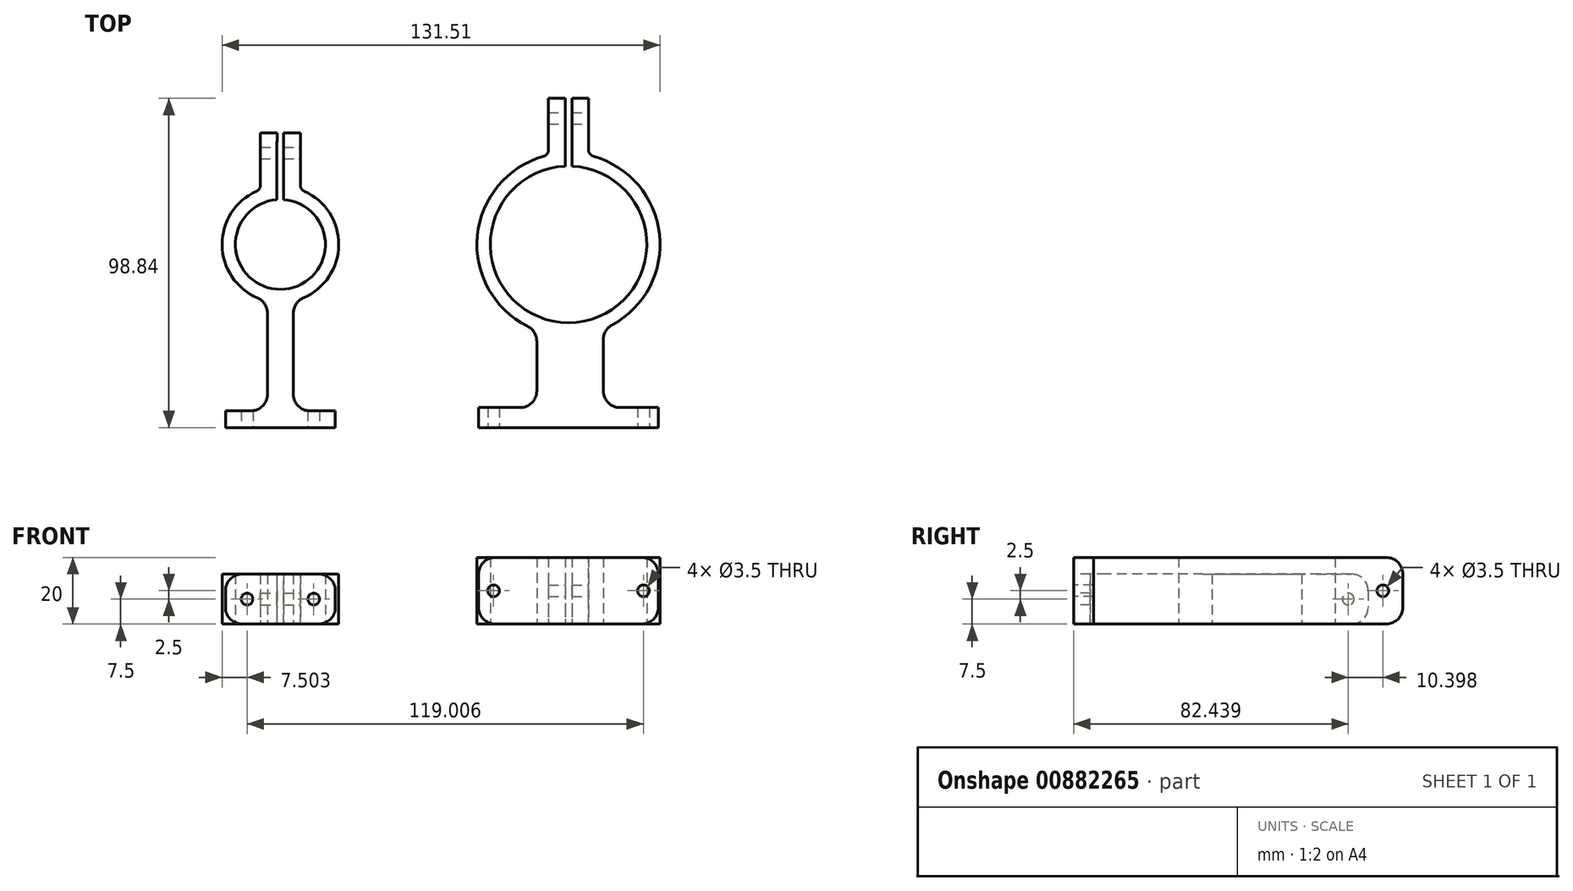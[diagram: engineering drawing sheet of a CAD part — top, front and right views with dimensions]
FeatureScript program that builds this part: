
annotation { "Feature Type Name" : "Feature", "Feature Type Description" : "" }
export const myFeature = defineFeature(function(context is Context, id is Id, definition is map)
    precondition{}
    {
        {
            var Q0;
            Q0=qCreatedBy(makeId("Top.planeOp"),FACE);
            var sketch = newSketch(context, id + "F0", { "sketchPlane" : qUnion([Q0])});
            skArc(sketch, "E0", {"start": v(-54.05, 13.46) * mm, "mid": v(-52.86, -13.5) * mm, "end": v(-52.05, 13.47) * mm});
            skArc(sketch, "E1", {"start": v(-46.04, -16.07) * mm, "mid": v(-35.46, 0.5) * mm, "end": v(-46.96, 16.44) * mm});
            skLineSegment(sketch, "E2.bottom", {"start": v(-69.46, -50) * mm, "end": v(-61.85, -50) * mm});
            skLineSegment(sketch, "E2.top", {"start": v(-69.46, -55) * mm, "end": v(-36.46, -55) * mm});
            skLineSegment(sketch, "E2.left", {"start": v(-69.46, -50) * mm, "end": v(-69.46, -55) * mm});
            skLineSegment(sketch, "E2.right", {"start": v(-36.46, -50) * mm, "end": v(-36.46, -55) * mm});
            skLineSegment(sketch, "E3", {"start": v(-52.96, 28.87) * mm, "end": v(-52.96, -56.44) * mm, "construction": true});
            skLineSegment(sketch, "E4.left", {"start": v(-56.85, -20.67) * mm, "end": v(-56.85, -45) * mm});
            skLineSegment(sketch, "E4.right", {"start": v(-49.06, -20.67) * mm, "end": v(-49.06, -45) * mm});
            skLineSegment(sketch, "E5.top", {"start": v(-46.96, 33.44) * mm, "end": v(-51.96, 33.44) * mm});
            skLineSegment(sketch, "E5.left", {"start": v(-46.96, 16.44) * mm, "end": v(-46.96, 33.44) * mm});
            skLineSegment(sketch, "E5.right", {"start": v(-58.96, 16.44) * mm, "end": v(-58.96, 33.44) * mm});
            skLineSegment(sketch, "E6.left", {"start": v(-53.96, 33.44) * mm, "end": v(-54.05, 13.46) * mm});
            skLineSegment(sketch, "E6.right", {"start": v(-51.96, 33.44) * mm, "end": v(-52.05, 13.47) * mm});
            skLineSegment(sketch, "E7.trimOffspring", {"start": v(-53.96, 33.44) * mm, "end": v(-58.96, 33.44) * mm});
            skArc(sketch, "E8.trimOffspring", {"start": v(-58.96, 16.44) * mm, "mid": v(-70.45, 0.5) * mm, "end": v(-59.88, -16.07) * mm});
            skLineSegment(sketch, "E9.trimOffspring", {"start": v(-44.06, -50) * mm, "end": v(-36.46, -50) * mm});
            skPoint(sketch, "E10.visualSharp", {"position": v(-56.85, -50) * mm});
            skArc(sketch, "E10.filletArc", {"start": v(-61.85, -50) * mm, "mid": v(-58.32, -48.54) * mm, "end": v(-56.85, -45) * mm});
            skPoint(sketch, "E11.visualSharp", {"position": v(-49.06, -50) * mm});
            skArc(sketch, "E11.filletArc", {"start": v(-49.06, -45) * mm, "mid": v(-47.6, -48.54) * mm, "end": v(-44.06, -50) * mm});
            skPoint(sketch, "E12.visualSharp", {"position": v(-49.06, -17.06) * mm});
            skArc(sketch, "E12.filletArc", {"start": v(-46.04, -16.07) * mm, "mid": v(-48.24, -17.92) * mm, "end": v(-49.06, -20.67) * mm});
            skPoint(sketch, "E13.visualSharp", {"position": v(-56.85, -17.06) * mm});
            skArc(sketch, "E13.filletArc", {"start": v(-56.85, -20.67) * mm, "mid": v(-57.68, -17.92) * mm, "end": v(-59.88, -16.07) * mm});
            skSolve(sketch);
        }
        {
            var Q0;
            Q0 = qSketchRegion(id + "F0", true);
            extrude(context, id + "F1", {"entities" : qUnion([Q0]), "depth" : 15 * mm, "offsetDistance" : 25 * mm});
        }
        {
            var Q0;
            Q0=makeQuery(id+"F1.opExtrude","SWEPT_FACE",FACE,{"disambiguationData":[OSD([sQuery(id+"F0.wireOp",EDGE,"E2.top")])]});
            var sketch = newSketch(context, id + "F2", { "sketchPlane" : qUnion([Q0])});
            skCircle(sketch, "E14", {"center": v(-62.96, 7.5) * mm, "radius": 1.75 * mm});
            skPoint(sketch, "E14.centerSnap0", {"position": v(-69.46, 7.5) * mm});
            skCircle(sketch, "E15", {"center": v(-42.96, 7.5) * mm, "radius": 1.75 * mm});
            skPoint(sketch, "E15.centerSnap0", {"position": v(-36.46, 7.5) * mm});
            skLineSegment(sketch, "E16", {"start": v(-52.96, -5.39) * mm, "end": v(-52.96, 15.18) * mm, "construction": true});
            skPoint(sketch, "E16.startSnap0", {"position": v(-52.96, 0) * mm});
            skSolve(sketch);
        }
        {
            var Q0;
            Q0 = qSketchRegion(id + "F2", true);
            extrude(context, id + "F3", {"entities" : qUnion([Q0]), "operationType" : NewBodyOperationType.REMOVE, "oppositeDirection" : true, "depth" : 25 * mm, "offsetDistance" : 25 * mm});
        }
        {
            var Q0;
            Q0=makeQuery(id+"F1.opExtrude","SWEPT_FACE",FACE,{"disambiguationData":[OSD([sQuery(id+"F0.wireOp",EDGE,"E5.left")])]});
            var sketch = newSketch(context, id + "F4", { "sketchPlane" : qUnion([Q0])});
            skPoint(sketch, "E17.centerSnap0", {"position": v(24.94, 15) * mm});
            skPoint(sketch, "E17.centerSnap1", {"position": v(33.44, 7.5) * mm});
            skCircle(sketch, "E18", {"center": v(27.44, 7.5) * mm, "radius": 1.75 * mm});
            skSolve(sketch);
        }
        {
            var Q0;
            Q0 = qSketchRegion(id + "F4", true);
            extrude(context, id + "F5", {"entities" : qUnion([Q0]), "operationType" : NewBodyOperationType.REMOVE, "oppositeDirection" : true, "depth" : 25 * mm, "offsetDistance" : 25 * mm});
        }
        {
            var Q0;
            Q0=makeQuery(id+"F1.opExtrude","CAP_EDGE",EDGE,{"disambiguationData":[OSD([sQuery(id+"F0.wireOp",EDGE,"E5.top")])],"isStart":false});
            var Q1;
            Q1=makeQuery(id+"F1.opExtrude","CAP_EDGE",EDGE,{"disambiguationData":[OSD([sQuery(id+"F0.wireOp",EDGE,"E7.trimOffspring")])],"isStart":false});
            var Q2;
            Q2=makeQuery(id+"F1.opExtrude","CAP_EDGE",EDGE,{"disambiguationData":[OSD([sQuery(id+"F0.wireOp",EDGE,"E5.top")])],"isStart":true});
            var Q3;
            Q3=makeQuery(id+"F1.opExtrude","CAP_EDGE",EDGE,{"disambiguationData":[OSD([sQuery(id+"F0.wireOp",EDGE,"E7.trimOffspring")])],"isStart":true});
            var Q4;
            Q4=makeQuery(id+"F1.opExtrude","CAP_EDGE",EDGE,{"disambiguationData":[OSD([sQuery(id+"F0.wireOp",EDGE,"E2.right")])],"isStart":false});
            var Q5;
            Q5=makeQuery(id+"F1.opExtrude","CAP_EDGE",EDGE,{"disambiguationData":[OSD([sQuery(id+"F0.wireOp",EDGE,"E2.right")])],"isStart":true});
            var Q6;
            Q6=makeQuery(id+"F1.opExtrude","CAP_EDGE",EDGE,{"disambiguationData":[OSD([sQuery(id+"F0.wireOp",EDGE,"E2.left")])],"isStart":false});
            var Q7;
            Q7=makeQuery(id+"F1.opExtrude","CAP_EDGE",EDGE,{"disambiguationData":[OSD([sQuery(id+"F0.wireOp",EDGE,"E2.left")])],"isStart":true});
            fillet(context, id + "F6", {"entities" : qUnion([Q0, Q1, Q2, Q3, Q4, Q5, Q6, Q7]), "radius" : 5 * mm, "tangentPropagation" : true, "allowEdgeOverflow" : false});
        }
        {
            var Q0;
            Q0=qCreatedBy(makeId("Top.planeOp"),FACE);
            var sketch = newSketch(context, id + "F7", { "sketchPlane" : qUnion([Q0])});
            skArc(sketch, "E19", {"start": v(32.55, 23.48) * mm, "mid": v(33.55, -23.5) * mm, "end": v(34.55, 23.48) * mm});
            skArc(sketch, "E20", {"start": v(27.55, 26.84) * mm, "mid": v(33.55, -27.5) * mm, "end": v(39.55, 26.84) * mm});
            skLineSegment(sketch, "E21.bottom", {"start": v(6.55, -55) * mm, "end": v(60.55, -55) * mm});
            skLineSegment(sketch, "E21.top", {"start": v(6.55, -49) * mm, "end": v(24.01, -49) * mm});
            skLineSegment(sketch, "E21.left", {"start": v(6.55, -55) * mm, "end": v(6.55, -49) * mm});
            skLineSegment(sketch, "E21.right", {"start": v(60.55, -55) * mm, "end": v(60.55, -49) * mm});
            skLineSegment(sketch, "E22", {"start": v(33.55, 36.73) * mm, "end": v(33.55, -65.9) * mm, "construction": true});
            skLineSegment(sketch, "E23.top", {"start": v(27.55, 43.84) * mm, "end": v(32.55, 43.84) * mm});
            skLineSegment(sketch, "E23.left", {"start": v(27.55, 26.84) * mm, "end": v(27.55, 43.84) * mm});
            skLineSegment(sketch, "E23.right", {"start": v(39.55, 26.84) * mm, "end": v(39.55, 43.84) * mm});
            skLineSegment(sketch, "E24.left", {"start": v(32.55, 23.48) * mm, "end": v(32.55, 43.84) * mm});
            skLineSegment(sketch, "E24.right", {"start": v(34.55, 23.48) * mm, "end": v(34.55, 43.84) * mm});
            skLineSegment(sketch, "E25.left", {"start": v(24.01, -25.8) * mm, "end": v(24.01, -49) * mm});
            skLineSegment(sketch, "E25.right", {"start": v(44.01, -25.43) * mm, "end": v(44.01, -49) * mm});
            skLineSegment(sketch, "E26.trimOffspring", {"start": v(34.55, 43.84) * mm, "end": v(39.55, 43.84) * mm});
            skLineSegment(sketch, "E27.trimOffspring", {"start": v(44.01, -49) * mm, "end": v(60.55, -49) * mm});
            skSolve(sketch);
        }
        {
            var Q0;
            Q0 = qSketchRegion(id + "F7", true);
            extrude(context, id + "F8", {"entities" : qUnion([Q0]), "depth" : 20 * mm, "offsetDistance" : 25 * mm});
        }
        {
            var Q0;
            Q0=makeQuery(id+"F8.opExtrude","SWEPT_FACE",FACE,{"disambiguationData":[OSD([sQuery(id+"F7.wireOp",EDGE,"E23.right")])]});
            var sketch = newSketch(context, id + "F9", { "sketchPlane" : qUnion([Q0])});
            skPoint(sketch, "E28.centerSnap0", {"position": v(43.84, 10) * mm});
            skPoint(sketch, "E28.centerSnap1", {"position": v(35.34, 20) * mm});
            skCircle(sketch, "E29", {"center": v(37.84, 10) * mm, "radius": 1.75 * mm});
            skSolve(sketch);
        }
        {
            var Q0;
            Q0 = qSketchRegion(id + "F9", true);
            extrude(context, id + "F10", {"entities" : qUnion([Q0]), "operationType" : NewBodyOperationType.REMOVE, "oppositeDirection" : true, "depth" : 25 * mm, "offsetDistance" : 25 * mm});
        }
        {
            var Q0;
            Q0=makeQuery(id+"F8.opExtrude","SWEPT_FACE",FACE,{"disambiguationData":[OSD([sQuery(id+"F7.wireOp",EDGE,"E21.bottom")])]});
            var sketch = newSketch(context, id + "F11", { "sketchPlane" : qUnion([Q0])});
            skLineSegment(sketch, "E30", {"start": v(33.55, 31.88) * mm, "end": v(33.55, -13.66) * mm, "construction": true});
            skPoint(sketch, "E30.startSnap0", {"position": v(33.55, 20) * mm});
            skPoint(sketch, "E30.endSnap0", {"position": v(33.55, 0) * mm});
            skCircle(sketch, "E31", {"center": v(56.05, 10) * mm, "radius": 1.75 * mm});
            skPoint(sketch, "E31.centerSnap0", {"position": v(60.55, 10) * mm});
            skCircle(sketch, "E32", {"center": v(11.05, 10) * mm, "radius": 1.75 * mm});
            skPoint(sketch, "E32.centerSnap0", {"position": v(6.55, 10) * mm});
            skSolve(sketch);
        }
        {
            var Q0;
            Q0 = qSketchRegion(id + "F11", true);
            extrude(context, id + "F12", {"entities" : qUnion([Q0]), "operationType" : NewBodyOperationType.REMOVE, "oppositeDirection" : true, "depth" : 25 * mm, "offsetDistance" : 25 * mm});
        }
        {
            var Q0;
            Q0=makeQuery(id+"F8.opExtrude","SWEPT_EDGE",EDGE,{"disambiguationData":[OSD([sQuery(id+"F7.wireOp",EDGE,"E25.right"),sQuery(id+"F7.wireOp",EDGE,"E27.trimOffspring")])]});
            var Q1;
            Q1=makeQuery(id+"F8.opExtrude","SWEPT_EDGE",EDGE,{"disambiguationData":[OSD([sQuery(id+"F7.wireOp",EDGE,"E20"),sQuery(id+"F7.wireOp",EDGE,"E25.right")])]});
            var Q2;
            Q2=makeQuery(id+"F8.opExtrude","CAP_EDGE",EDGE,{"disambiguationData":[OSD([sQuery(id+"F7.wireOp",EDGE,"E21.right")])],"isStart":false});
            var Q3;
            Q3=makeQuery(id+"F8.opExtrude","CAP_EDGE",EDGE,{"disambiguationData":[OSD([sQuery(id+"F7.wireOp",EDGE,"E26.trimOffspring")])],"isStart":false});
            var Q4;
            Q4=makeQuery(id+"F8.opExtrude","CAP_EDGE",EDGE,{"disambiguationData":[OSD([sQuery(id+"F7.wireOp",EDGE,"E23.top")])],"isStart":false});
            var Q5;
            Q5=makeQuery(id+"F8.opExtrude","CAP_EDGE",EDGE,{"disambiguationData":[OSD([sQuery(id+"F7.wireOp",EDGE,"E21.right")])],"isStart":true});
            var Q6;
            Q6=makeQuery(id+"F8.opExtrude","CAP_EDGE",EDGE,{"disambiguationData":[OSD([sQuery(id+"F7.wireOp",EDGE,"E26.trimOffspring")])],"isStart":true});
            var Q7;
            Q7=makeQuery(id+"F8.opExtrude","CAP_EDGE",EDGE,{"disambiguationData":[OSD([sQuery(id+"F7.wireOp",EDGE,"E23.top")])],"isStart":true});
            var Q8;
            Q8=makeQuery(id+"F8.opExtrude","CAP_EDGE",EDGE,{"disambiguationData":[OSD([sQuery(id+"F7.wireOp",EDGE,"E21.left")])],"isStart":true});
            var Q9;
            Q9=makeQuery(id+"F8.opExtrude","CAP_EDGE",EDGE,{"disambiguationData":[OSD([sQuery(id+"F7.wireOp",EDGE,"E21.left")])],"isStart":false});
            var Q10;
            Q10=makeQuery(id+"F8.opExtrude","SWEPT_EDGE",EDGE,{"disambiguationData":[OSD([sQuery(id+"F7.wireOp",EDGE,"E20"),sQuery(id+"F7.wireOp",EDGE,"E25.left")])]});
            fillet(context, id + "F13", {"entities" : qUnion([Q0, Q1, Q2, Q3, Q4, Q5, Q6, Q7, Q8, Q9, Q10]), "radius" : 5 * mm, "tangentPropagation" : true, "allowEdgeOverflow" : false});
        }
        {
            var Q0;
            Q0=makeQuery(id+"F8.opExtrude","SWEPT_EDGE",EDGE,{"disambiguationData":[OSD([sQuery(id+"F7.wireOp",EDGE,"E20"),sQuery(id+"F7.wireOp",EDGE,"E23.left")])]});
            var Q1;
            Q1=makeQuery(id+"F1.opExtrude","SWEPT_EDGE",EDGE,{"disambiguationData":[OSD([sQuery(id+"F0.wireOp",EDGE,"E5.right"),sQuery(id+"F0.wireOp",EDGE,"E8.trimOffspring")])]});
            var Q2;
            Q2=makeQuery(id+"F8.opExtrude","SWEPT_EDGE",EDGE,{"disambiguationData":[OSD([sQuery(id+"F7.wireOp",EDGE,"E20"),sQuery(id+"F7.wireOp",EDGE,"E23.right")])]});
            var Q3;
            Q3=makeQuery(id+"F1.opExtrude","SWEPT_EDGE",EDGE,{"disambiguationData":[OSD([sQuery(id+"F0.wireOp",EDGE,"E1"),sQuery(id+"F0.wireOp",EDGE,"E5.left")])]});
            fillet(context, id + "F14", {"entities" : qUnion([Q0, Q1, Q2, Q3]), "radius" : 2 * mm, "tangentPropagation" : true, "allowEdgeOverflow" : false});
        }
        {
            var Q0;
            Q0=makeQuery(id+"F8.opExtrude","SWEPT_EDGE",EDGE,{"disambiguationData":[OSD([sQuery(id+"F7.wireOp",EDGE,"E21.top"),sQuery(id+"F7.wireOp",EDGE,"E25.left")])]});
            fillet(context, id + "F15", {"entities" : qUnion([Q0]), "radius" : 5 * mm, "tangentPropagation" : true, "allowEdgeOverflow" : false});
        }
    });
